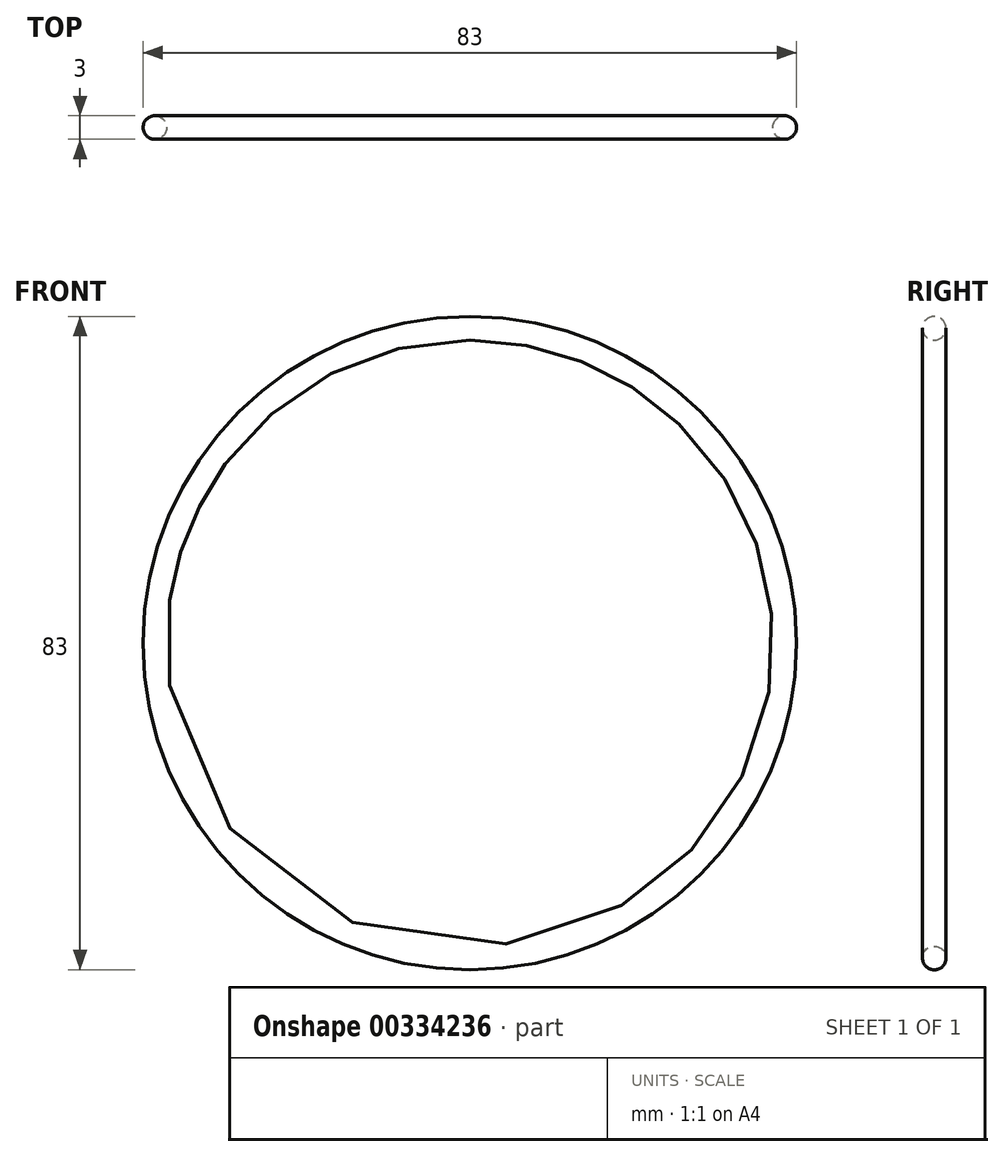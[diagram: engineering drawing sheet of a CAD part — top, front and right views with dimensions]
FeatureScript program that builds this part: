
annotation { "Feature Type Name" : "Feature", "Feature Type Description" : "" }
export const myFeature = defineFeature(function(context is Context, id is Id, definition is map)
    precondition{}
    {
        {
            var Q0;
            Q0=qCreatedBy(makeId("Front.planeOp"),FACE);
            var sketch = newSketch(context, id + "F0", { "sketchPlane" : qUnion([Q0])});
            skCircle(sketch, "E0", {"center": v(0, 0) * mm, "radius": 40 * mm});
            skSolve(sketch);
        }
        {
            var Q0;
            Q0=qCreatedBy(makeId("Right.planeOp"),FACE);
            var sketch = newSketch(context, id + "F1", { "sketchPlane" : qUnion([Q0])});
            skCircle(sketch, "E1", {"center": v(0, 40) * mm, "radius": 1.5 * mm});
            skSolve(sketch);
        }
        {
            var Q0;
            Q0=makeQuery(id+"F1.imprint","IMPRINT",FACE,{"disambiguationData":[TD([[makeQuery(id+"F1.imprint","IMPRINT",EDGE,{"derivedFrom":sQuery(id+"F1.wireOp",EDGE,"E1")}),1.0]])]});
            var Q1;
            Q1=sQuery(id+"F0.wireOp",EDGE,"E0");
            revolve(context, id + "F2", {"entities" : qUnion([Q0]), "axis" : qUnion([Q1]), "revolveType" : RevolveType.FULL});
        }
    });
